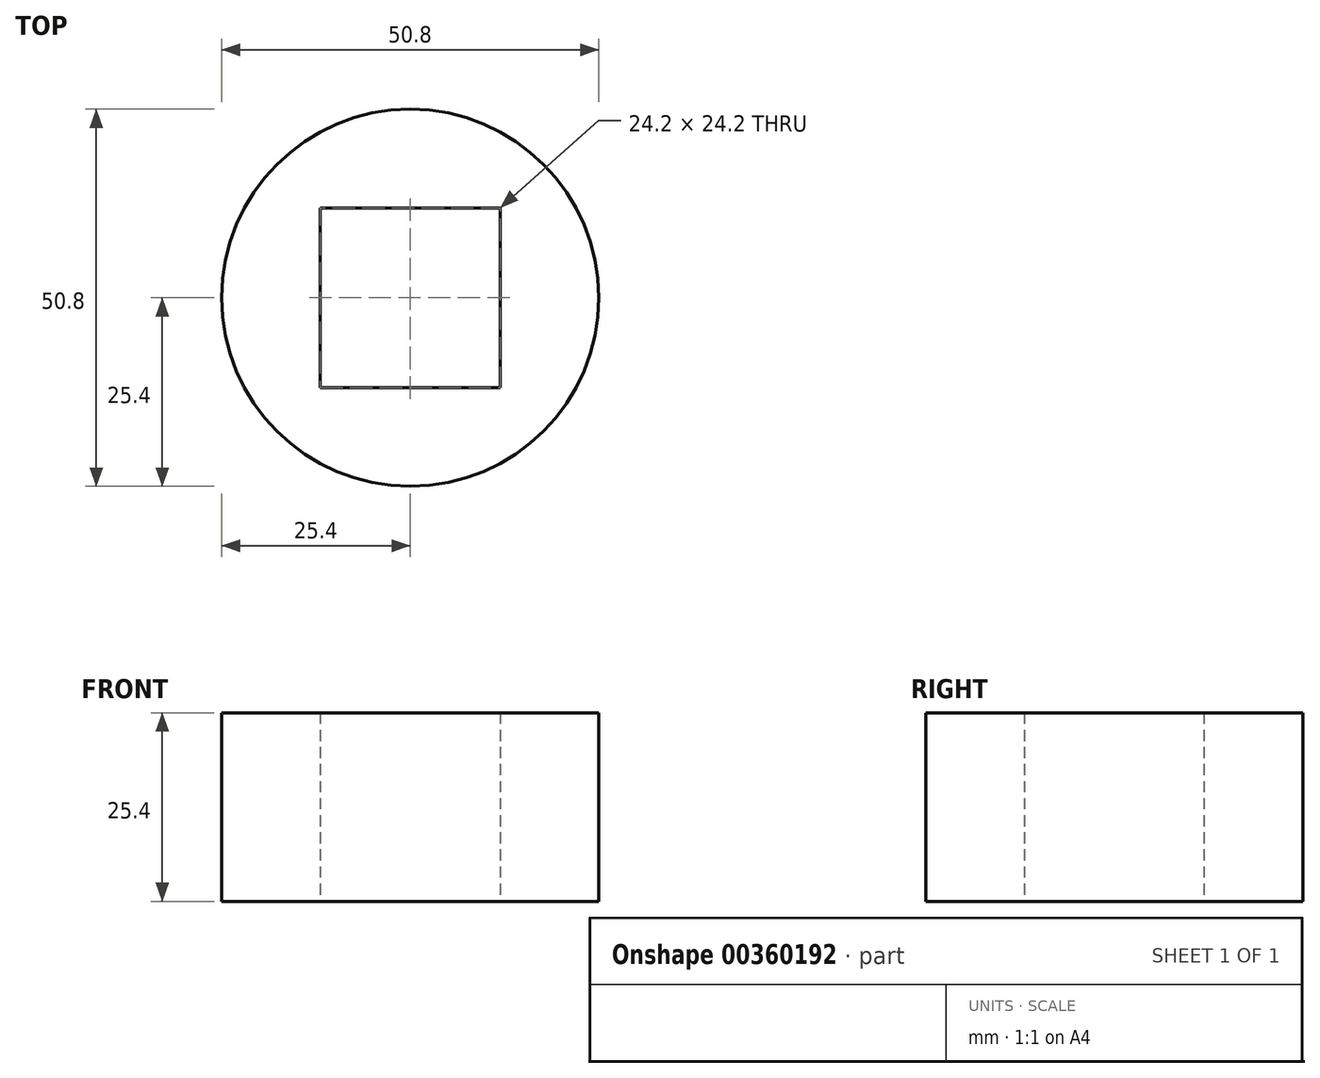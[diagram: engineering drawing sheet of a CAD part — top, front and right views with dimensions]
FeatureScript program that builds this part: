
annotation { "Feature Type Name" : "Feature", "Feature Type Description" : "" }
export const myFeature = defineFeature(function(context is Context, id is Id, definition is map)
    precondition{}
    {
        {
            var Q0;
            Q0=qCreatedBy(makeId("Top.planeOp"),FACE);
            var sketch = newSketch(context, id + "F0", { "sketchPlane" : qUnion([Q0])});
            skCircle(sketch, "E0", {"center": v(0, 0) * mm, "radius": 25.4 * mm});
            skLineSegment(sketch, "E1.bottom", {"start": v(12.1, 12.1) * mm, "end": v(-12.1, 12.1) * mm});
            skLineSegment(sketch, "E1.top", {"start": v(12.1, -12.1) * mm, "end": v(-12.1, -12.1) * mm});
            skLineSegment(sketch, "E1.left", {"start": v(12.1, 12.1) * mm, "end": v(12.1, -12.1) * mm});
            skLineSegment(sketch, "E1.right", {"start": v(-12.1, 12.1) * mm, "end": v(-12.1, -12.1) * mm});
            skSolve(sketch);
        }
        {
            var Q0;
            Q0=makeQuery(id+"F0.imprint","IMPRINT",FACE,{"disambiguationData":[TD([[makeQuery(id+"F0.imprint","IMPRINT",EDGE,{"derivedFrom":sQuery(id+"F0.wireOp",EDGE,"E0")}),1.0]])]});
            extrude(context, id + "F1", {"entities" : qUnion([Q0]), "depth" : 25.4 * mm});
        }
    });
